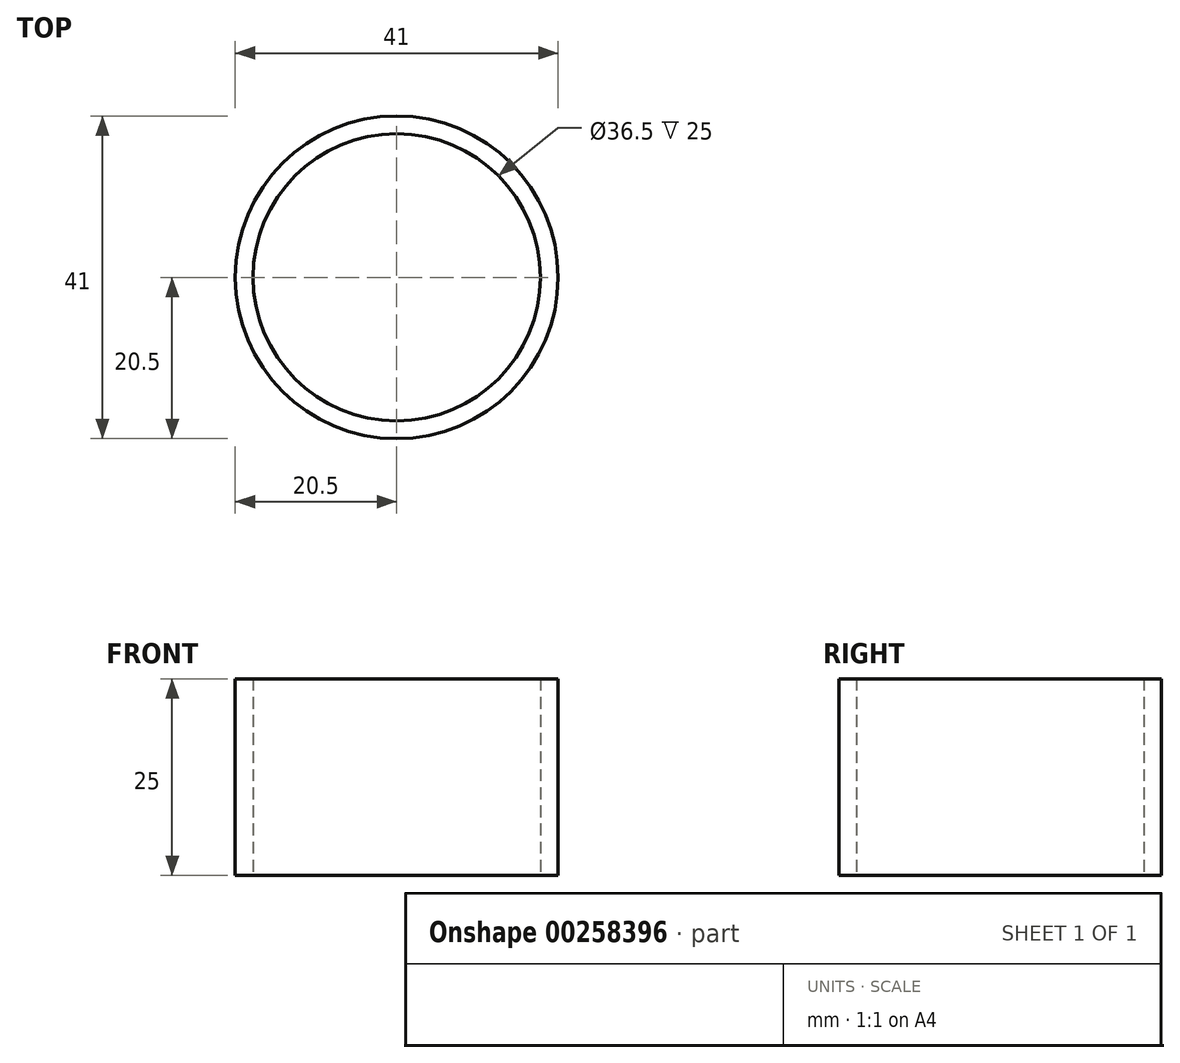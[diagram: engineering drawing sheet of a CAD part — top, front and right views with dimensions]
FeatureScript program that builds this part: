
annotation { "Feature Type Name" : "Feature", "Feature Type Description" : "" }
export const myFeature = defineFeature(function(context is Context, id is Id, definition is map)
    precondition{}
    {
        {
            var Q0;
            Q0=qCreatedBy(makeId("Top.planeOp"),FACE);
            var sketch = newSketch(context, id + "F0", { "sketchPlane" : qUnion([Q0])});
            skCircle(sketch, "E0", {"center": v(0, 0) * mm, "radius": 20.5 * mm});
            skCircle(sketch, "E1", {"center": v(0, 0) * mm, "radius": 18.25 * mm});
            skSolve(sketch);
        }
        {
            var Q0;
            Q0=makeQuery(id+"F0.imprint","IMPRINT",FACE,{"disambiguationData":[TD([[makeQuery(id+"F0.imprint","IMPRINT",EDGE,{"derivedFrom":sQuery(id+"F0.wireOp",EDGE,"E0")}),1.0]])]});
            extrude(context, id + "F1", {"entities" : qUnion([Q0]), "depth" : 25 * mm});
        }
    });
